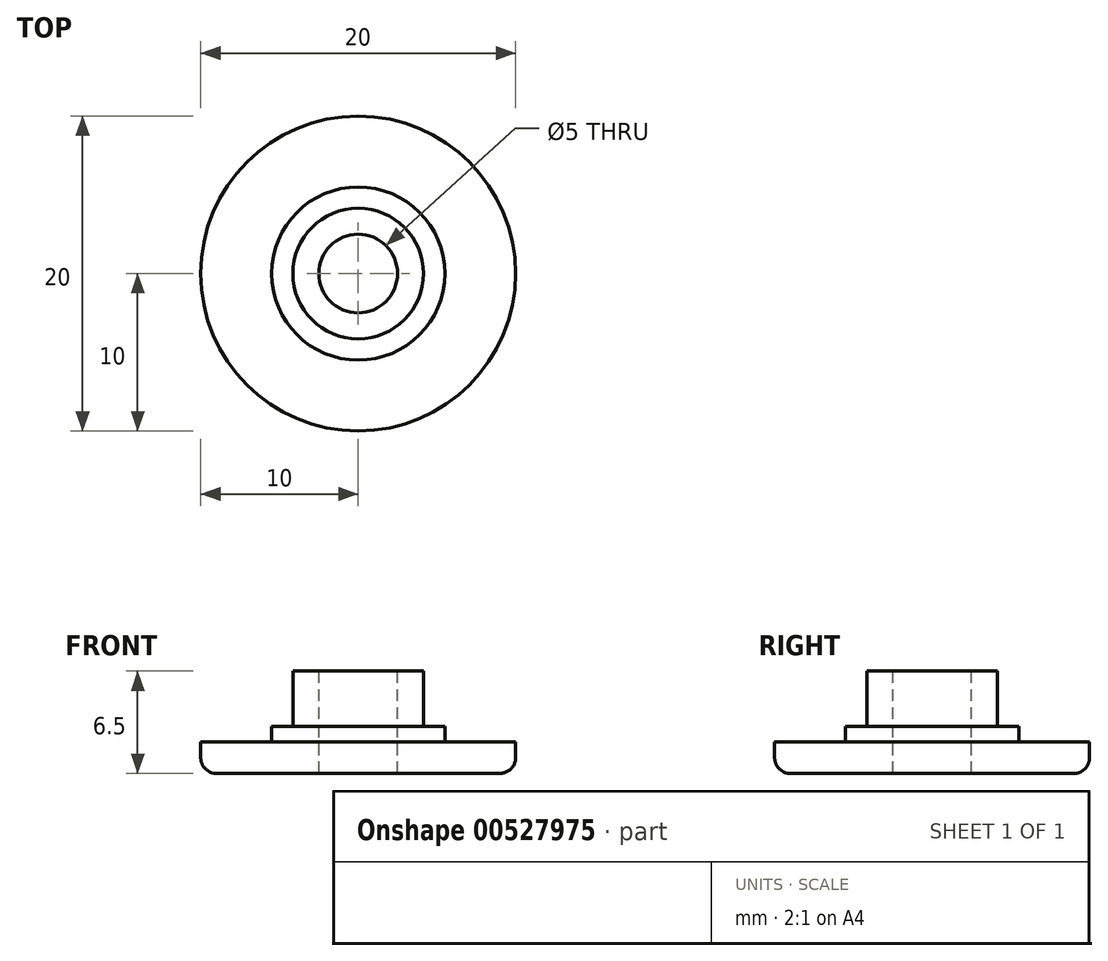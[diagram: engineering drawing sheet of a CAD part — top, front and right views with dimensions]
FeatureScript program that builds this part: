
annotation { "Feature Type Name" : "Feature", "Feature Type Description" : "" }
export const myFeature = defineFeature(function(context is Context, id is Id, definition is map)
    precondition{}
    {
        {
            var Q0;
            Q0=qCreatedBy(makeId("Top.planeOp"),FACE);
            var sketch = newSketch(context, id + "F0", { "sketchPlane" : qUnion([Q0])});
            skCircle(sketch, "E0", {"center": v(0, 0) * mm, "radius": 10 * mm});
            skSolve(sketch);
        }
        {
            var Q0;
            Q0=makeQuery(id+"F0.imprint","IMPRINT",FACE,{"disambiguationData":[TD([[makeQuery(id+"F0.imprint","IMPRINT",EDGE,{"derivedFrom":sQuery(id+"F0.wireOp",EDGE,"E0")}),1.0]])]});
            extrude(context, id + "F1", {"entities" : qUnion([Q0]), "depth" : 2 * mm, "offsetDistance" : 25 * mm});
        }
        {
            var Q0;
            Q0=makeQuery(id+"F1.opExtrude","CAP_FACE",FACE,{"disambiguationData":[OSD([sQuery(id+"F0.wireOp",EDGE,"E0")])],"isStart":false});
            var sketch = newSketch(context, id + "F2", { "sketchPlane" : qUnion([Q0])});
            skCircle(sketch, "E1", {"center": v(0, 0) * mm, "radius": 5.5 * mm});
            skSolve(sketch);
        }
        {
            var Q0;
            Q0=makeQuery(id+"F2.imprint","IMPRINT",FACE,{"disambiguationData":[TD([[makeQuery(id+"F2.imprint","IMPRINT",EDGE,{"derivedFrom":sQuery(id+"F2.wireOp",EDGE,"E1")}),1.0]])]});
            extrude(context, id + "F3", {"entities" : qUnion([Q0]), "operationType" : NewBodyOperationType.ADD, "depth" : 1 * mm, "offsetDistance" : 25 * mm});
        }
        {
            var Q0;
            Q0=makeQuery(id+"F3.opExtrude","CAP_FACE",FACE,{"disambiguationData":[OSD([sQuery(id+"F2.wireOp",EDGE,"E1")])],"isStart":false});
            var sketch = newSketch(context, id + "F4", { "sketchPlane" : qUnion([Q0])});
            skCircle(sketch, "E2", {"center": v(0, 0) * mm, "radius": 4.15 * mm});
            skSolve(sketch);
        }
        {
            var Q0;
            Q0 = qSketchRegion(id + "F4", true);
            extrude(context, id + "F5", {"entities" : qUnion([Q0]), "operationType" : NewBodyOperationType.ADD, "depth" : 3.5 * mm, "offsetDistance" : 25 * mm});
        }
        {
            var Q0;
            Q0=makeQuery(id+"F5.opExtrude","CAP_FACE",FACE,{"disambiguationData":[OSD([sQuery(id+"F4.wireOp",EDGE,"E2")])],"isStart":false});
            var sketch = newSketch(context, id + "F6", { "sketchPlane" : qUnion([Q0])});
            skCircle(sketch, "E3", {"center": v(0, 0) * mm, "radius": 2.5 * mm});
            skSolve(sketch);
        }
        {
            var Q0;
            Q0=makeQuery(id+"F6.imprint","IMPRINT",FACE,{"disambiguationData":[TD([[makeQuery(id+"F6.imprint","IMPRINT",EDGE,{"derivedFrom":sQuery(id+"F6.wireOp",EDGE,"E3")}),1.0]])]});
            extrude(context, id + "F7", {"entities" : qUnion([Q0]), "operationType" : NewBodyOperationType.REMOVE, "oppositeDirection" : true, "depth" : 10 * mm, "offsetDistance" : 25 * mm});
        }
        {
            var Q0;
            Q0=makeQuery(id+"F1.opExtrude","CAP_EDGE",EDGE,{"disambiguationData":[OSD([sQuery(id+"F0.wireOp",EDGE,"E0")])],"isStart":true});
            fillet(context, id + "F8", {"entities" : qUnion([Q0]), "radius" : 1 * mm, "tangentPropagation" : true, "allowEdgeOverflow" : false});
        }
    });
